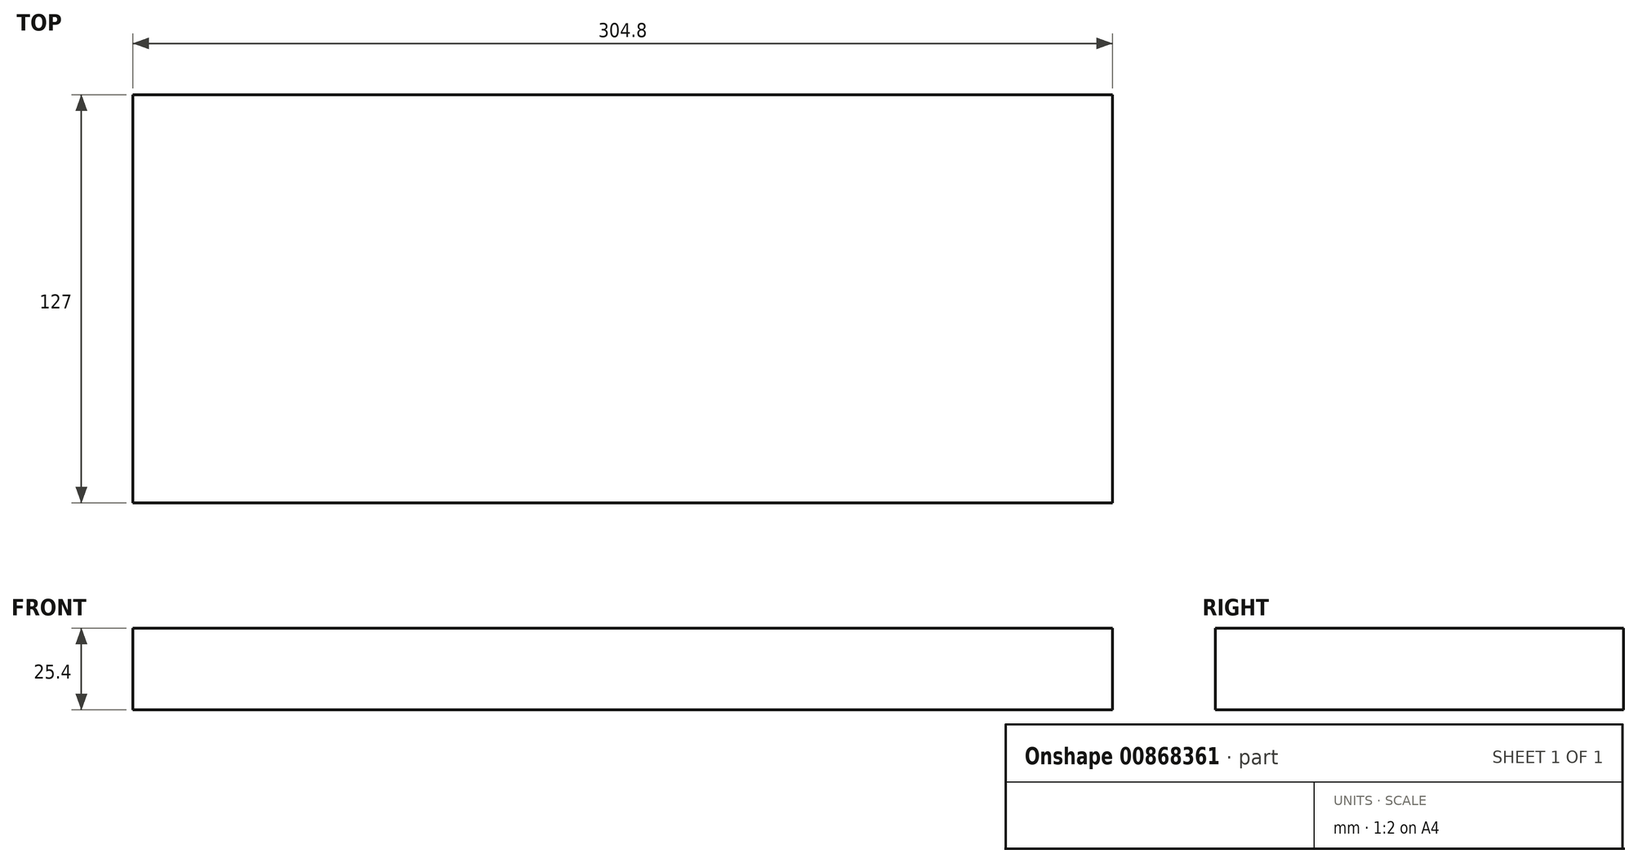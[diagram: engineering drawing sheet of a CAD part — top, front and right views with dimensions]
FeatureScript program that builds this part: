
annotation { "Feature Type Name" : "Feature", "Feature Type Description" : "" }
export const myFeature = defineFeature(function(context is Context, id is Id, definition is map)
    precondition{}
    {
        {
            var Q0;
            Q0=qCreatedBy(makeId("Top.planeOp"),FACE);
            var sketch = newSketch(context, id + "F0", { "sketchPlane" : qUnion([Q0])});
            skLineSegment(sketch, "E0.bottom", {"start": v(152.4, 63.5) * mm, "end": v(-152.4, 63.5) * mm});
            skLineSegment(sketch, "E0.top", {"start": v(152.4, -63.5) * mm, "end": v(-152.4, -63.5) * mm});
            skLineSegment(sketch, "E0.left", {"start": v(152.4, 63.5) * mm, "end": v(152.4, -63.5) * mm});
            skLineSegment(sketch, "E0.right", {"start": v(-152.4, 63.5) * mm, "end": v(-152.4, -63.5) * mm});
            skPoint(sketch, "E0.middle", {"position": v(0, 0) * mm});
            skSolve(sketch);
        }
        {
            var Q0;
            Q0=makeQuery(id+"F0.imprint","IMPRINT",FACE,{"disambiguationData":[TD([[makeQuery(id+"F0.imprint","IMPRINT",EDGE,{"derivedFrom":sQuery(id+"F0.wireOp",EDGE,"E0.bottom")}),1.0]])]});
            extrude(context, id + "F1", {"entities" : qUnion([Q0]), "depth" : 25.4 * mm, "offsetDistance" : 25.4 * mm});
        }
    });
